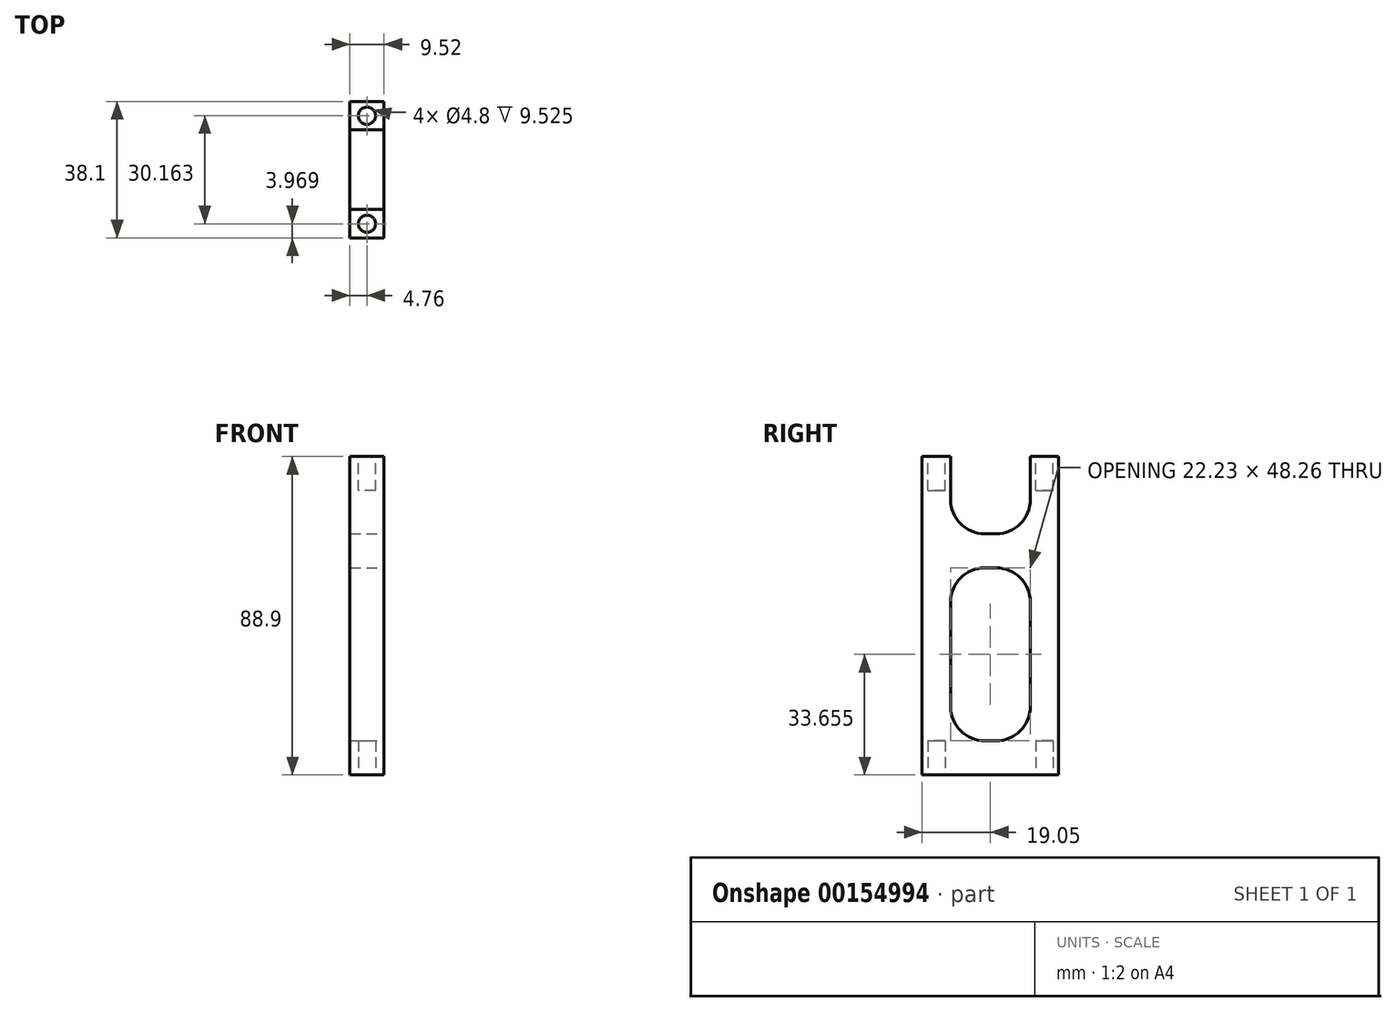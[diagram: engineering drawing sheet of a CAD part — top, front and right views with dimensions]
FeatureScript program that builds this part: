
annotation { "Feature Type Name" : "Feature", "Feature Type Description" : "" }
export const myFeature = defineFeature(function(context is Context, id is Id, definition is map)
    precondition{}
    {
        {
            var Q0;
            Q0=qCreatedBy(makeId("Right.planeOp"),FACE);
            var sketch = newSketch(context, id + "F0", { "sketchPlane" : qUnion([Q0])});
            skLineSegment(sketch, "E0.bottom", {"start": v(0, 0) * mm, "end": v(38.1, 0) * mm});
            skLineSegment(sketch, "E0.top", {"start": v(0, 88.9) * mm, "end": v(38.1, 88.9) * mm});
            skLineSegment(sketch, "E0.left", {"start": v(0, 0) * mm, "end": v(0, 88.9) * mm});
            skLineSegment(sketch, "E0.right", {"start": v(38.1, 0) * mm, "end": v(38.1, 88.9) * mm});
            skSolve(sketch);
        }
        {
            var Q0;
            Q0 = qSketchRegion(id + "F0", true);
            extrude(context, id + "F1", {"entities" : qUnion([Q0]), "depth" : 9.52 * mm, "symmetric" : true});
        }
        {
            var Q0;
            Q0=makeQuery(id+"F1.opExtrude","CAP_FACE",FACE,{"disambiguationData":[OSD([sQuery(id+"F0.wireOp",EDGE,"E0.bottom"),sQuery(id+"F0.wireOp",EDGE,"E0.top"),sQuery(id+"F0.wireOp",EDGE,"E0.left"),sQuery(id+"F0.wireOp",EDGE,"E0.right")])],"isStart":false});
            var sketch = newSketch(context, id + "F2", { "sketchPlane" : qUnion([Q0])});
            skLineSegment(sketch, "E1", {"start": v(19.05, 0) * mm, "end": v(19.05, 117.7) * mm, "construction": true});
            skLineSegment(sketch, "E2", {"start": v(7.94, 88.9) * mm, "end": v(30.16, 88.9) * mm});
            skPoint(sketch, "E3", {"position": v(19.05, 88.9) * mm});
            skLineSegment(sketch, "E4", {"start": v(7.94, 88.9) * mm, "end": v(7.94, 76.84) * mm});
            skLineSegment(sketch, "E5", {"start": v(17.46, 67.31) * mm, "end": v(20.64, 67.31) * mm});
            skLineSegment(sketch, "E6", {"start": v(30.16, 88.9) * mm, "end": v(30.16, 76.84) * mm});
            skPoint(sketch, "E7.visualSharp", {"position": v(7.94, 67.31) * mm});
            skArc(sketch, "E7.filletArc", {"start": v(7.94, 76.84) * mm, "mid": v(10.73, 70.1) * mm, "end": v(17.46, 67.31) * mm});
            skPoint(sketch, "E8.visualSharp", {"position": v(30.16, 67.31) * mm});
            skArc(sketch, "E8.filletArc", {"start": v(20.64, 67.31) * mm, "mid": v(27.37, 70.1) * mm, "end": v(30.16, 76.84) * mm});
            skSolve(sketch);
        }
        {
            var Q0;
            Q0 = qSketchRegion(id + "F2", true);
            extrude(context, id + "F3", {"entities" : qUnion([Q0]), "operationType" : NewBodyOperationType.REMOVE, "oppositeDirection" : true, "depth" : 25.4 * mm, "symmetric" : true});
        }
        {
            var Q0;
            {var subQ1=sQuery(id+"F0.wireOp",EDGE,"E0.left");var subQ2=sQuery(id+"F0.wireOp",EDGE,"E0.top");Q0=makeQuery(id+"F3.boolean.opBoolean","SPLIT",FACE,{"disambiguationData":[TD([makeQuery(id+"F1.opExtrude","SWEPT_FACE",FACE,{"disambiguationData":[OSD([subQ1])]})])],"derivedFrom":makeQuery(id+"F1.opExtrude","SWEPT_FACE",FACE,{"disambiguationData":[OSD([subQ2])]})});}
            var sketch = newSketch(context, id + "F4", { "sketchPlane" : qUnion([Q0])});
            skCircle(sketch, "E9", {"center": v(0, 3.97) * mm, "radius": 2.4 * mm});
            skCircle(sketch, "E10", {"center": v(0, 34.13) * mm, "radius": 2.4 * mm});
            skSolve(sketch);
        }
        {
            var Q0;
            Q0 = qSketchRegion(id + "F4", true);
            extrude(context, id + "F5", {"entities" : qUnion([Q0]), "operationType" : NewBodyOperationType.REMOVE, "oppositeDirection" : true, "depth" : 9.52 * mm});
        }
        {
            var Q0;
            Q0=makeQuery(id+"F1.opExtrude","SWEPT_FACE",FACE,{"disambiguationData":[OSD([sQuery(id+"F0.wireOp",EDGE,"E0.bottom")])]});
            var sketch = newSketch(context, id + "F6", { "sketchPlane" : qUnion([Q0])});
            skCircle(sketch, "E11.0", {"center": v(0, -3.97) * mm, "radius": 2.4 * mm});
            skCircle(sketch, "E12.0", {"center": v(0, -34.13) * mm, "radius": 2.4 * mm});
            skSolve(sketch);
        }
        {
            var Q0;
            Q0 = qSketchRegion(id + "F6", true);
            extrude(context, id + "F7", {"entities" : qUnion([Q0]), "operationType" : NewBodyOperationType.REMOVE, "oppositeDirection" : true, "depth" : 9.52 * mm});
        }
        {
            var Q0;
            Q0=makeQuery(id+"F1.opExtrude","CAP_FACE",FACE,{"disambiguationData":[OSD([sQuery(id+"F0.wireOp",EDGE,"E0.bottom"),sQuery(id+"F0.wireOp",EDGE,"E0.top"),sQuery(id+"F0.wireOp",EDGE,"E0.left"),sQuery(id+"F0.wireOp",EDGE,"E0.right")])],"isStart":false});
            var sketch = newSketch(context, id + "F8", { "sketchPlane" : qUnion([Q0])});
            skLineSegment(sketch, "E13", {"start": v(7.94, 76.84) * mm, "end": v(7.94, 0) * mm, "construction": true});
            skLineSegment(sketch, "E14", {"start": v(30.16, 76.84) * mm, "end": v(30.16, 0) * mm, "construction": true});
            skLineSegment(sketch, "E15.bottom", {"start": v(7.94, 57.79) * mm, "end": v(30.16, 57.79) * mm});
            skLineSegment(sketch, "E15.top", {"start": v(7.94, 9.53) * mm, "end": v(30.16, 9.53) * mm});
            skLineSegment(sketch, "E15.left", {"start": v(7.94, 57.79) * mm, "end": v(7.94, 9.52) * mm});
            skLineSegment(sketch, "E15.right", {"start": v(30.16, 57.79) * mm, "end": v(30.16, 9.52) * mm});
            skSolve(sketch);
        }
        {
            var Q0;
            Q0 = qSketchRegion(id + "F8", true);
            extrude(context, id + "F9", {"entities" : qUnion([Q0]), "operationType" : NewBodyOperationType.REMOVE, "endBound" : BoundingType.THROUGH_ALL, "oppositeDirection" : true, "depth" : 25.4 * mm});
        }
        {
            var Q0;
            Q0=makeQuery(id+"F9.boolean.opBoolean","COPY",EDGE,{"derivedFrom":makeQuery(id+"F9.opExtrude","SWEPT_EDGE",EDGE,{"disambiguationData":[OSD([sQuery(id+"F8.wireOp",EDGE,"E15.bottom"),sQuery(id+"F8.wireOp",EDGE,"E15.left")])]})});
            var Q1;
            Q1=makeQuery(id+"F9.boolean.opBoolean","COPY",EDGE,{"derivedFrom":makeQuery(id+"F9.opExtrude","SWEPT_EDGE",EDGE,{"disambiguationData":[OSD([sQuery(id+"F8.wireOp",EDGE,"E15.bottom"),sQuery(id+"F8.wireOp",EDGE,"E15.right")])]})});
            var Q2;
            Q2=makeQuery(id+"F9.boolean.opBoolean","COPY",EDGE,{"derivedFrom":makeQuery(id+"F9.opExtrude","SWEPT_EDGE",EDGE,{"disambiguationData":[OSD([sQuery(id+"F8.wireOp",EDGE,"E15.top"),sQuery(id+"F8.wireOp",EDGE,"E15.left")])]})});
            var Q3;
            Q3=makeQuery(id+"F9.boolean.opBoolean","COPY",EDGE,{"derivedFrom":makeQuery(id+"F9.opExtrude","SWEPT_EDGE",EDGE,{"disambiguationData":[OSD([sQuery(id+"F8.wireOp",EDGE,"E15.top"),sQuery(id+"F8.wireOp",EDGE,"E15.right")])]})});
            fillet(context, id + "F10", {"entities" : qUnion([Q0, Q1, Q2, Q3]), "radius" : 9.52 * mm, "tangentPropagation" : true, "allowEdgeOverflow" : false});
        }
    });
